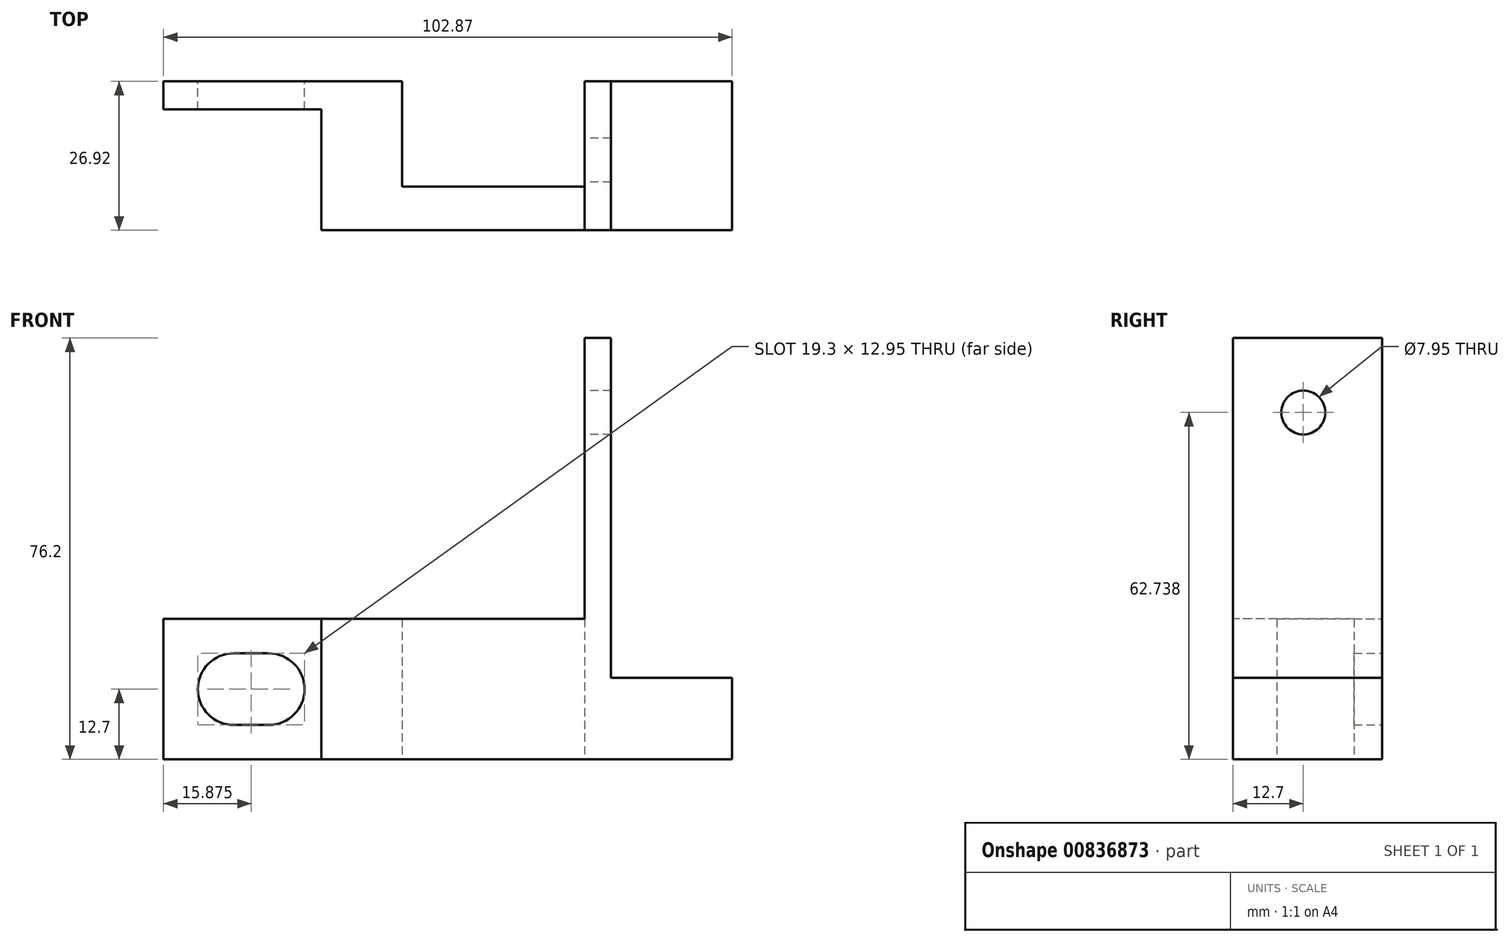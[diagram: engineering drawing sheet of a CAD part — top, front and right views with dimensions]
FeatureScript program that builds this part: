
annotation { "Feature Type Name" : "Feature", "Feature Type Description" : "" }
export const myFeature = defineFeature(function(context is Context, id is Id, definition is map)
    precondition{}
    {
        {
            var Q0;
            Q0=qCreatedBy(makeId("Top.planeOp"),FACE);
            var sketch = newSketch(context, id + "F0", { "sketchPlane" : qUnion([Q0])});
            skLineSegment(sketch, "E0.bottom", {"start": v(0, 0) * mm, "end": v(-74.3, 0) * mm});
            skLineSegment(sketch, "E0.top", {"start": v(0, 26.92) * mm, "end": v(-26.67, 26.92) * mm});
            skLineSegment(sketch, "E0.left", {"start": v(0, 0) * mm, "end": v(0, 26.92) * mm});
            skLineSegment(sketch, "E0.right", {"start": v(-102.87, 21.84) * mm, "end": v(-102.87, 26.92) * mm});
            skLineSegment(sketch, "E1", {"start": v(-102.87, 21.84) * mm, "end": v(-74.3, 21.84) * mm});
            skLineSegment(sketch, "E2", {"start": v(-26.67, 26.92) * mm, "end": v(-26.67, 7.87) * mm});
            skLineSegment(sketch, "E3", {"start": v(-26.67, 7.87) * mm, "end": v(-59.7, 7.87) * mm});
            skLineSegment(sketch, "E4", {"start": v(-59.7, 7.87) * mm, "end": v(-59.7, 26.92) * mm});
            skLineSegment(sketch, "E5.trimOffspring", {"start": v(-59.7, 26.92) * mm, "end": v(-102.87, 26.92) * mm});
            skLineSegment(sketch, "E6", {"start": v(-74.3, 21.84) * mm, "end": v(-74.3, 0) * mm});
            skSolve(sketch);
        }
        {
            var Q0;
            Q0 = qSketchRegion(id + "F0", true);
            extrude(context, id + "F1", {"entities" : qUnion([Q0]), "depth" : 25.4 * mm, "offsetDistance" : 25.4 * mm});
        }
        {
            var Q0;
            Q0=makeQuery(id+"F1.opExtrude","SWEPT_FACE",FACE,{"disambiguationData":[OSD([sQuery(id+"F0.wireOp",EDGE,"E5.trimOffspring")])]});
            var sketch = newSketch(context, id + "F2", { "sketchPlane" : qUnion([Q0])});
            skArc(sketch, "E7", {"start": v(90.17, 6.22) * mm, "mid": v(96.65, 12.7) * mm, "end": v(90.17, 19.18) * mm});
            skLineSegment(sketch, "E8", {"start": v(90.17, 12.7) * mm, "end": v(90.17, 25.4) * mm, "construction": true});
            skLineSegment(sketch, "E9", {"start": v(90.17, 12.7) * mm, "end": v(90.17, 0) * mm, "construction": true});
            skLineSegment(sketch, "E10.bottom", {"start": v(90.17, 19.18) * mm, "end": v(83.82, 19.18) * mm});
            skLineSegment(sketch, "E10.top", {"start": v(90.17, 6.22) * mm, "end": v(83.82, 6.22) * mm});
            skLineSegment(sketch, "E10.left", {"start": v(90.17, 19.18) * mm, "end": v(90.17, 6.22) * mm});
            skArc(sketch, "E11", {"start": v(83.82, 19.18) * mm, "mid": v(77.34, 12.7) * mm, "end": v(83.82, 6.22) * mm});
            skSolve(sketch);
        }
        {
            var Q0;
            Q0 = qSketchRegion(id + "F2", true);
            extrude(context, id + "F3", {"entities" : qUnion([Q0]), "operationType" : NewBodyOperationType.REMOVE, "oppositeDirection" : true, "depth" : 127 * mm, "offsetDistance" : 25.4 * mm});
        }
        {
            var Q0;
            Q0=makeQuery(id+"F1.opExtrude","CAP_FACE",FACE,{"disambiguationData":[OSD([sQuery(id+"F0.wireOp",EDGE,"E0.bottom"),sQuery(id+"F0.wireOp",EDGE,"E0.top"),sQuery(id+"F0.wireOp",EDGE,"E0.left"),sQuery(id+"F0.wireOp",EDGE,"E0.right"),sQuery(id+"F0.wireOp",EDGE,"E1"),sQuery(id+"F0.wireOp",EDGE,"E2"),sQuery(id+"F0.wireOp",EDGE,"E3"),sQuery(id+"F0.wireOp",EDGE,"E4"),sQuery(id+"F0.wireOp",EDGE,"E5.trimOffspring"),sQuery(id+"F0.wireOp",EDGE,"E6")])],"isStart":false});
            var sketch = newSketch(context, id + "F4", { "sketchPlane" : qUnion([Q0])});
            skLineSegment(sketch, "E12.bottom", {"start": v(-26.67, 26.92) * mm, "end": v(-21.9, 26.92) * mm});
            skLineSegment(sketch, "E12.top", {"start": v(-26.67, 0) * mm, "end": v(-21.9, 0) * mm});
            skLineSegment(sketch, "E12.left", {"start": v(-26.67, 26.92) * mm, "end": v(-26.67, 0) * mm});
            skLineSegment(sketch, "E12.right", {"start": v(-21.9, 26.92) * mm, "end": v(-21.9, 0) * mm});
            skSolve(sketch);
        }
        {
            var Q0;
            Q0 = qSketchRegion(id + "F4", true);
            extrude(context, id + "F5", {"entities" : qUnion([Q0]), "operationType" : NewBodyOperationType.ADD, "depth" : 50.8 * mm, "offsetDistance" : 25.4 * mm});
        }
        {
            var Q0;
            Q0=makeQuery(id+"F5.boolean.opBoolean","MERGE",FACE,{"derivedFrom":[makeQuery(id+"F1.opExtrude","SWEPT_FACE",FACE,{"disambiguationData":[OSD([sQuery(id+"F0.wireOp",EDGE,"E2")])]}),makeQuery(id+"F5.opExtrude","SWEPT_FACE",FACE,{"disambiguationData":[OSD([sQuery(id+"F4.wireOp",EDGE,"E12.left")])]})]});
            var sketch = newSketch(context, id + "F6", { "sketchPlane" : qUnion([Q0])});
            skCircle(sketch, "E13", {"center": v(-12.7, 62.74) * mm, "radius": 3.98 * mm});
            skSolve(sketch);
        }
        {
            var Q0;
            Q0 = qSketchRegion(id + "F6", true);
            extrude(context, id + "F7", {"entities" : qUnion([Q0]), "operationType" : NewBodyOperationType.REMOVE, "oppositeDirection" : true, "depth" : 25.4 * mm, "offsetDistance" : 25.4 * mm});
        }
        {
            var Q0;
            Q0=makeQuery(id+"F5.opExtrude","SWEPT_FACE",FACE,{"disambiguationData":[OSD([sQuery(id+"F4.wireOp",EDGE,"E12.right")])]});
            var sketch = newSketch(context, id + "F8", { "sketchPlane" : qUnion([Q0])});
            skLineSegment(sketch, "E14.bottom", {"start": v(0, 76.2) * mm, "end": v(26.92, 76.2) * mm});
            skLineSegment(sketch, "E14.top", {"start": v(0, 18.72) * mm, "end": v(26.92, 18.72) * mm});
            skLineSegment(sketch, "E14.left", {"start": v(0, 76.2) * mm, "end": v(0, 18.72) * mm});
            skLineSegment(sketch, "E14.right", {"start": v(26.92, 76.2) * mm, "end": v(26.92, 18.72) * mm});
            skSolve(sketch);
        }
        {
            var Q0;
            Q0 = qSketchRegion(id + "F8", true);
            extrude(context, id + "F9", {"entities" : qUnion([Q0]), "operationType" : NewBodyOperationType.REMOVE, "depth" : 25.4 * mm, "offsetDistance" : 25.4 * mm});
        }
        {
            var Q0;
            Q0=makeQuery(id+"F9.boolean.opBoolean","COPY",FACE,{"derivedFrom":makeQuery(id+"F9.opExtrude","SWEPT_FACE",FACE,{"disambiguationData":[OSD([sQuery(id+"F8.wireOp",EDGE,"E14.top")])]})});
            var sketch = newSketch(context, id + "F10", { "sketchPlane" : qUnion([Q0])});
            skLineSegment(sketch, "E15.bottom", {"start": v(0, 26.92) * mm, "end": v(-21.9, 26.92) * mm});
            skLineSegment(sketch, "E15.top", {"start": v(0, 0) * mm, "end": v(-21.9, 0) * mm});
            skLineSegment(sketch, "E15.left", {"start": v(0, 26.92) * mm, "end": v(0, 0) * mm});
            skLineSegment(sketch, "E15.right", {"start": v(-21.9, 26.92) * mm, "end": v(-21.9, 0) * mm});
            skSolve(sketch);
        }
        {
            var Q0;
            Q0 = qSketchRegion(id + "F10", true);
            extrude(context, id + "F11", {"entities" : qUnion([Q0]), "operationType" : NewBodyOperationType.REMOVE, "oppositeDirection" : true, "depth" : 4 * mm, "offsetDistance" : 25.4 * mm});
        }
    });
